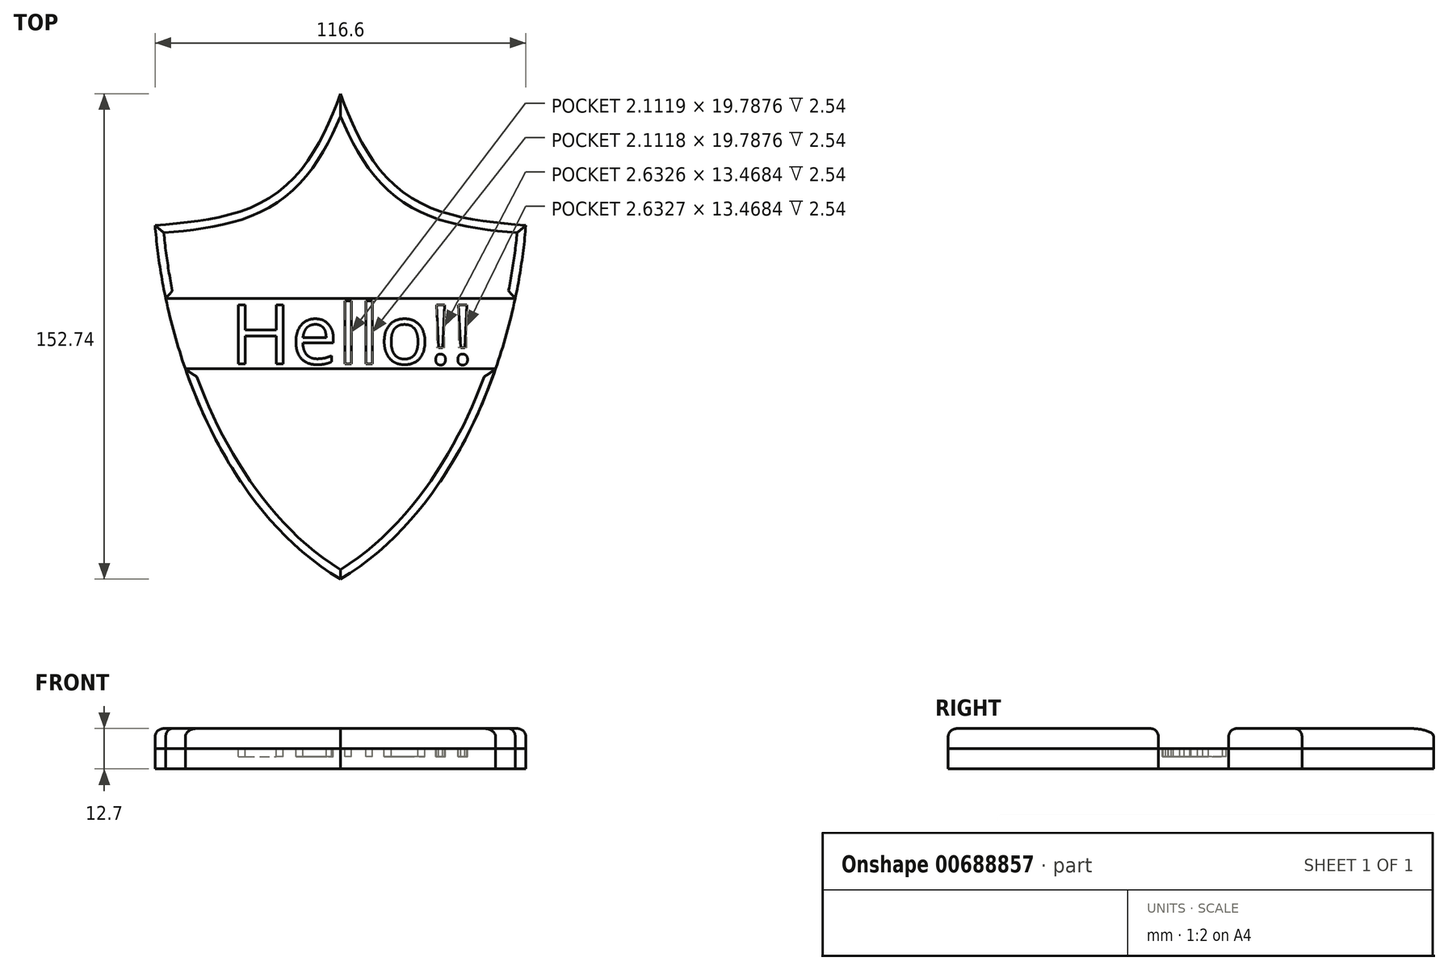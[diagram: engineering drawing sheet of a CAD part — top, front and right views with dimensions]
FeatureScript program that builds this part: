
annotation { "Feature Type Name" : "Feature", "Feature Type Description" : "" }
export const myFeature = defineFeature(function(context is Context, id is Id, definition is map)
    precondition{}
    {
        {
            var Q0;
            Q0=qCreatedBy(makeId("Top.planeOp"),FACE);
            var sketch = newSketch(context, id + "F0", { "sketchPlane" : qUnion([Q0])});
            skFitSpline(sketch, "E0", {"points": [v(-58.3, 34.46) * mm, v(0, -76.84) * mm], "startDerivative": vector(9.21, -122.38) * mm, "endDerivative": vector(107.4, -63.54) * mm});
            skFitSpline(sketch, "E1", {"points": [v(-58.3, 34.46) * mm, v(0, 75.9) * mm], "startDerivative": vector(91.22, 6.97) * mm, "endDerivative": vector(37, 104.01) * mm});
            skFitSpline(sketch, "E2.MirrorCS", {"points": [v(58.3, 34.46) * mm, v(0, -76.84) * mm], "startDerivative": vector(-9.21, -122.38) * mm, "endDerivative": vector(-107.4, -63.54) * mm});
            skFitSpline(sketch, "E3.MirrorCS", {"points": [v(58.3, 34.46) * mm, v(0, 75.9) * mm], "startDerivative": vector(-91.22, 6.97) * mm, "endDerivative": vector(-37, 104.01) * mm});
            skLineSegment(sketch, "E4", {"start": v(-54.96, 11.4) * mm, "end": v(54.96, 11.4) * mm});
            skLineSegment(sketch, "E5", {"start": v(-48.8, -10.7) * mm, "end": v(48.8, -10.7) * mm});
            skSolve(sketch);
        }
        {
            var Q0;
            {var subQ3=sQuery(id+"F0.wireOp",EDGE,"E1");Q0=makeQuery(id+"F0.imprint","IMPRINT",FACE,{"disambiguationData":[TD([[makeQuery(id+"F0.imprint","IMPRINT",EDGE,{"derivedFrom":subQ3}),-1.0]])]});}
            var Q1;
            {var subQ3=sQuery(id+"F0.wireOp",EDGE,"E5");Q1=makeQuery(id+"F0.imprint","IMPRINT",FACE,{"disambiguationData":[TD([[makeQuery(id+"F0.imprint","IMPRINT",EDGE,{"derivedFrom":subQ3}),-1.0]])]});}
            extrude(context, id + "F1", {"entities" : qUnion([Q0, Q1]), "depth" : 12.7 * mm, "offsetDistance" : 25.4 * mm});
        }
        {
            var Q0;
            Q0 = qSketchRegion(id + "F0", true);
            extrude(context, id + "F2", {"entities" : qUnion([Q0]), "depth" : 6.35 * mm, "offsetDistance" : 25.4 * mm});
        }
        {
            var Q0;
            Q0=makeQuery(id+"F2.opExtrude","CAP_FACE",FACE,{"disambiguationData":[OSD([sQuery(id+"F0.wireOp",EDGE,"E0"),sQuery(id+"F0.wireOp",EDGE,"E1"),sQuery(id+"F0.wireOp",EDGE,"E2.MirrorCS"),sQuery(id+"F0.wireOp",EDGE,"E3.MirrorCS")])],"isStart":false});
            var sketch = newSketch(context, id + "F3", { "sketchPlane" : qUnion([Q0])});
            skText(sketch, "E6", { "text": "Hello!!", "fontName": "OpenSans-Regular.ttf"});
            const initialGuessF3  = {"E6": [-0.0347, -0.00913, 1, 0, 0.01875]};
            skSetInitialGuess(sketch, initialGuessF3);
            skSolve(sketch);
        }
        {
            var Q0;
            Q0 = qSketchRegion(id + "F3", true);
            extrude(context, id + "F4", {"entities" : qUnion([Q0]), "operationType" : NewBodyOperationType.REMOVE, "oppositeDirection" : true, "depth" : 2.54 * mm, "offsetDistance" : 25.4 * mm});
        }
        {
            var Q0;
            Q0=makeQuery(id+"F1.opExtrude","CAP_FACE",FACE,{"disambiguationData":[OSD([sQuery(id+"F0.wireOp",EDGE,"E0"),sQuery(id+"F0.wireOp",EDGE,"E1"),sQuery(id+"F0.wireOp",EDGE,"E2.MirrorCS"),sQuery(id+"F0.wireOp",EDGE,"E3.MirrorCS"),sQuery(id+"F0.wireOp",EDGE,"E4")])],"isStart":false});
            fillet(context, id + "F5", {"entities" : qUnion([Q0]), "radius" : 2.54 * mm, "tangentPropagation" : true, "allowEdgeOverflow" : false});
        }
        {
            var Q0;
            Q0=makeQuery(id+"F1.opExtrude","CAP_FACE",FACE,{"disambiguationData":[OSD([sQuery(id+"F0.wireOp",EDGE,"E0"),sQuery(id+"F0.wireOp",EDGE,"E2.MirrorCS"),sQuery(id+"F0.wireOp",EDGE,"E5")])],"isStart":false});
            fillet(context, id + "F6", {"entities" : qUnion([Q0]), "radius" : 2.54 * mm, "tangentPropagation" : true, "allowEdgeOverflow" : false});
        }
    });
